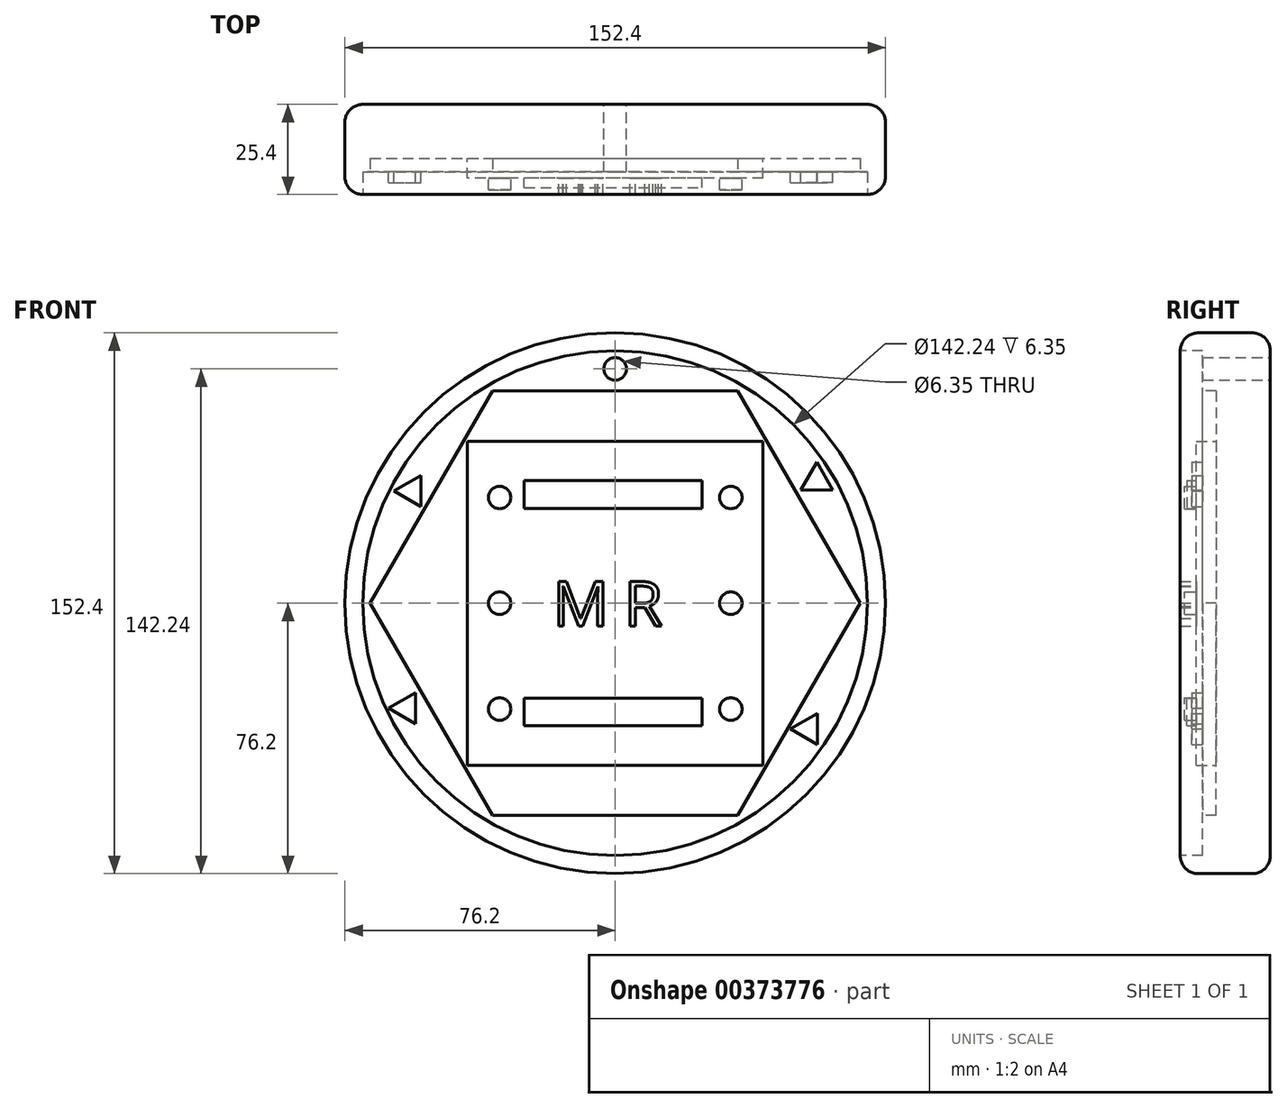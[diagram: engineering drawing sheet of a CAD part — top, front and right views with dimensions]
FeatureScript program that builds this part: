
annotation { "Feature Type Name" : "Feature", "Feature Type Description" : "" }
export const myFeature = defineFeature(function(context is Context, id is Id, definition is map)
    precondition{}
    {
        {
            var Q0;
            Q0=qCreatedBy(makeId("Front.planeOp"),FACE);
            var sketch = newSketch(context, id + "F0", { "sketchPlane" : qUnion([Q0])});
            skCircle(sketch, "E0", {"center": v(0, 0) * mm, "radius": 76.2 * mm});
            skSolve(sketch);
        }
        {
            var Q0;
            Q0 = qSketchRegion(id + "F0", true);
            extrude(context, id + "F1", {"entities" : qUnion([Q0]), "depth" : 25.4 * mm});
        }
        {
            var Q0;
            Q0=makeQuery(id+"F1.opExtrude","CAP_EDGE",EDGE,{"disambiguationData":[OSD([sQuery(id+"F0.wireOp",EDGE,"E0")])],"isStart":false});
            var Q1;
            Q1=makeQuery(id+"F1.opExtrude","CAP_EDGE",EDGE,{"disambiguationData":[OSD([sQuery(id+"F0.wireOp",EDGE,"E0")])],"isStart":true});
            fillet(context, id + "F2", {"entities" : qUnion([Q0, Q1]), "radius" : 5.08 * mm, "tangentPropagation" : true, "allowEdgeOverflow" : false});
        }
        {
            var Q0;
            Q0=makeQuery(id+"F1.opExtrude","CAP_FACE",FACE,{"disambiguationData":[OSD([sQuery(id+"F0.wireOp",EDGE,"E0")])],"isStart":false});
            extrude(context, id + "F3", {"entities" : qUnion([Q0]), "operationType" : NewBodyOperationType.REMOVE, "oppositeDirection" : true, "depth" : 6.35 * mm});
        }
        {
            var Q0;
            Q0=makeQuery(id+"F3.boolean.opBoolean","COPY",FACE,{"derivedFrom":makeQuery(id+"F3.opExtrude","CAP_FACE",FACE,{"disambiguationData":[OSD([sQuery(id+"F0.wireOp",EDGE,"E0")])],"isStart":false})});
            var sketch = newSketch(context, id + "F4", { "sketchPlane" : qUnion([Q0])});
            skText(sketch, "E1", { "text": "M", "fontName": "OpenSans-Regular.ttf"});
            const initialGuessF4  = {"E1": [-0.01767, -0.00645, 1, 0, 0.0127]};
            skSetInitialGuess(sketch, initialGuessF4);
            skSolve(sketch);
        }
        {
            var Q0;
            Q0=makeQuery(id+"F3.boolean.opBoolean","COPY",FACE,{"derivedFrom":makeQuery(id+"F3.opExtrude","CAP_FACE",FACE,{"disambiguationData":[OSD([sQuery(id+"F0.wireOp",EDGE,"E0")])],"isStart":false})});
            var sketch = newSketch(context, id + "F5", { "sketchPlane" : qUnion([Q0])});
            skText(sketch, "E2", { "text": "R", "fontName": "OpenSans-Regular.ttf"});
            const initialGuessF5  = {"E2": [0.0025, -0.00648, 1, 0, 0.0127]};
            skSetInitialGuess(sketch, initialGuessF5);
            skSolve(sketch);
        }
        {
            var Q0;
            Q0=qCreatedBy(makeId("Front.planeOp"),FACE);
            var sketch = newSketch(context, id + "F6", { "sketchPlane" : qUnion([Q0])});
            skCircle(sketch, "E3", {"center": v(0, 66.04) * mm, "radius": 3.18 * mm});
            skSolve(sketch);
        }
        {
            var Q0;
            Q0=sQuery(id+"F6.wireOp",VERTEX,"E3.center");
            var Q1;
            Q1=makeQuery(id+"F1.opExtrude","SWEPT_BODY",BODY,{"disambiguationData":[OSD([sQuery(id+"F0.wireOp",EDGE,"E0")])]});
            hole(context, id + "F7", {"style" : HoleStyle.SIMPLE, "endStyle" : HoleEndStyle.THROUGH, "oppositeDirection" : true, "holeDiameter" : 6.35 * mm, "isTappedThrough" : true, "tappedDepth" : 12.7 * mm, "tapClearance" : 3, "locations" : qUnion([Q0]), "scope" : qUnion([Q1])});
        }
        {
            var Q0;
            Q0=makeQuery(id+"F3.boolean.opBoolean","COPY",FACE,{"derivedFrom":makeQuery(id+"F3.opExtrude","CAP_FACE",FACE,{"disambiguationData":[OSD([sQuery(id+"F0.wireOp",EDGE,"E0")])],"isStart":false})});
            var sketch = newSketch(context, id + "F8", { "sketchPlane" : qUnion([Q0])});
            skCircle(sketch, "E4", {"center": v(-32.59, -29.81) * mm, "radius": 3.18 * mm});
            skCircle(sketch, "E5", {"center": v(-32.59, 0) * mm, "radius": 3.18 * mm});
            skCircle(sketch, "E6", {"center": v(-32.59, 29.82) * mm, "radius": 3.18 * mm});
            skCircle(sketch, "E7", {"center": v(32.59, -29.82) * mm, "radius": 3.18 * mm});
            skCircle(sketch, "E8", {"center": v(32.59, 0) * mm, "radius": 3.18 * mm});
            skCircle(sketch, "E9", {"center": v(32.59, 29.82) * mm, "radius": 3.18 * mm});
            skSolve(sketch);
        }
        {
            var Q0;
            Q0 = qSketchRegion(id + "F8", true);
            extrude(context, id + "F9", {"entities" : qUnion([Q0]), "depth" : 5.08 * mm, "offsetDistance" : 25.4 * mm});
        }
        {
            var Q0;
            Q0=qCreatedBy(makeId("Front.planeOp"),FACE);
            var sketch = newSketch(context, id + "F10", { "sketchPlane" : qUnion([Q0])});
            skCircle(sketch, "E10.cCircle", {"center": v(0, 0) * mm, "radius": 59.82 * mm, "construction": true});
            skLineSegment(sketch, "E10.0", {"start": v(34.54, 59.82) * mm, "end": v(69.08, 0) * mm});
            skLineSegment(sketch, "E10.1", {"start": v(69.08, 0) * mm, "end": v(34.54, -59.82) * mm});
            skLineSegment(sketch, "E10.2", {"start": v(34.54, -59.82) * mm, "end": v(-34.54, -59.82) * mm});
            skLineSegment(sketch, "E10.3", {"start": v(-34.54, -59.82) * mm, "end": v(-69.08, 0) * mm});
            skLineSegment(sketch, "E10.4", {"start": v(-69.08, 0) * mm, "end": v(-34.54, 59.82) * mm});
            skLineSegment(sketch, "E10.5", {"start": v(-34.54, 59.82) * mm, "end": v(34.54, 59.82) * mm});
            skPoint(sketch, "E10.0.midPoint", {"position": v(51.8, 29.91) * mm});
            skSolve(sketch);
        }
        {
            var Q0;
            Q0 = qSketchRegion(id + "F10", true);
            extrude(context, id + "F11", {"entities" : qUnion([Q0]), "operationType" : NewBodyOperationType.ADD, "depth" : 20.32 * mm});
        }
        {
            var Q0;
            Q0=qCreatedBy(makeId("Front.planeOp"),FACE);
            var sketch = newSketch(context, id + "F12", { "sketchPlane" : qUnion([Q0])});
            skLineSegment(sketch, "E11.bottom", {"start": v(41.68, -45.62) * mm, "end": v(-41.68, -45.62) * mm});
            skLineSegment(sketch, "E11.top", {"start": v(41.68, 45.62) * mm, "end": v(-41.68, 45.62) * mm});
            skLineSegment(sketch, "E11.left", {"start": v(41.68, -45.62) * mm, "end": v(41.68, 45.62) * mm});
            skLineSegment(sketch, "E11.right", {"start": v(-41.68, -45.62) * mm, "end": v(-41.68, 45.62) * mm});
            skPoint(sketch, "E11.middle", {"position": v(0, 0) * mm});
            skSolve(sketch);
        }
        {
            var Q0;
            Q0 = qSketchRegion(id + "F12", true);
            extrude(context, id + "F13", {"entities" : qUnion([Q0]), "operationType" : NewBodyOperationType.ADD, "depth" : 20.83 * mm, "offsetDistance" : 25.4 * mm});
        }
        {
            var Q0;
            Q0=qCreatedBy(makeId("Front.planeOp"),FACE);
            var sketch = newSketch(context, id + "F14", { "sketchPlane" : qUnion([Q0])});
            skCircle(sketch, "E12.cCircle", {"center": v(56.84, 34.54) * mm, "radius": 2.62 * mm, "construction": true});
            skLineSegment(sketch, "E12.0", {"start": v(61.38, 31.92) * mm, "end": v(52.3, 31.92) * mm});
            skLineSegment(sketch, "E12.1", {"start": v(52.3, 31.92) * mm, "end": v(56.84, 39.79) * mm});
            skLineSegment(sketch, "E12.2", {"start": v(56.84, 39.79) * mm, "end": v(61.38, 31.92) * mm});
            skPoint(sketch, "E12.0.midPoint", {"position": v(56.84, 31.92) * mm});
            skSolve(sketch);
        }
        {
            var Q0;
            Q0 = qSketchRegion(id + "F14", true);
            extrude(context, id + "F15", {"entities" : qUnion([Q0]), "operationType" : NewBodyOperationType.ADD, "depth" : 22.1 * mm});
        }
        {
            var Q0;
            Q0=qCreatedBy(makeId("Front.planeOp"),FACE);
            var sketch = newSketch(context, id + "F16", { "sketchPlane" : qUnion([Q0])});
            skCircle(sketch, "E13.cCircle", {"center": v(54.46, -35.41) * mm, "radius": 2.54 * mm, "construction": true});
            skLineSegment(sketch, "E13.0", {"start": v(57, -31.01) * mm, "end": v(57, -39.81) * mm});
            skLineSegment(sketch, "E13.1", {"start": v(57, -39.81) * mm, "end": v(49.38, -35.41) * mm});
            skLineSegment(sketch, "E13.2", {"start": v(49.38, -35.41) * mm, "end": v(57, -31.01) * mm});
            skPoint(sketch, "E13.0.midPoint", {"position": v(57, -35.41) * mm});
            skSolve(sketch);
        }
        {
            var Q0;
            Q0 = qSketchRegion(id + "F16", true);
            extrude(context, id + "F17", {"entities" : qUnion([Q0]), "operationType" : NewBodyOperationType.ADD, "depth" : 22.1 * mm});
        }
        {
            var Q0;
            Q0=qCreatedBy(makeId("Front.planeOp"),FACE);
            var sketch = newSketch(context, id + "F18", { "sketchPlane" : qUnion([Q0])});
            skCircle(sketch, "E14.cCircle", {"center": v(-57.32, 31.63) * mm, "radius": 2.54 * mm, "construction": true});
            skLineSegment(sketch, "E14.0", {"start": v(-54.78, 36.02) * mm, "end": v(-54.78, 27.23) * mm});
            skLineSegment(sketch, "E14.1", {"start": v(-54.78, 27.23) * mm, "end": v(-62.4, 31.63) * mm});
            skLineSegment(sketch, "E14.2", {"start": v(-62.4, 31.63) * mm, "end": v(-54.78, 36.02) * mm});
            skPoint(sketch, "E14.0.midPoint", {"position": v(-54.78, 31.63) * mm});
            skSolve(sketch);
        }
        {
            var Q0;
            Q0 = qSketchRegion(id + "F18", true);
            extrude(context, id + "F19", {"entities" : qUnion([Q0]), "operationType" : NewBodyOperationType.ADD, "depth" : 22.1 * mm});
        }
        {
            var Q0;
            Q0=qCreatedBy(makeId("Front.planeOp"),FACE);
            var sketch = newSketch(context, id + "F20", { "sketchPlane" : qUnion([Q0])});
            skCircle(sketch, "E15.cCircle", {"center": v(-58.77, -29.58) * mm, "radius": 2.54 * mm, "construction": true});
            skLineSegment(sketch, "E15.0", {"start": v(-56.23, -25.19) * mm, "end": v(-56.23, -33.98) * mm});
            skLineSegment(sketch, "E15.1", {"start": v(-56.23, -33.98) * mm, "end": v(-63.85, -29.58) * mm});
            skLineSegment(sketch, "E15.2", {"start": v(-63.85, -29.58) * mm, "end": v(-56.23, -25.19) * mm});
            skPoint(sketch, "E15.0.midPoint", {"position": v(-56.23, -29.58) * mm});
            skSolve(sketch);
        }
        {
            var Q0;
            Q0 = qSketchRegion(id + "F20", true);
            extrude(context, id + "F21", {"entities" : qUnion([Q0]), "operationType" : NewBodyOperationType.ADD, "depth" : 22.1 * mm});
        }
        {
            var Q0;
            {var subQ0=sQuery(id+"F10.wireOp",EDGE,"E10.0");var subQ1=sQuery(id+"F10.wireOp",EDGE,"E10.1");var subQ2=sQuery(id+"F10.wireOp",EDGE,"E10.4");var subQ3=sQuery(id+"F10.wireOp",EDGE,"E10.2");var subQ4=sQuery(id+"F10.wireOp",EDGE,"E10.3");var subQ5=sQuery(id+"F10.wireOp",EDGE,"E10.5");Q0=makeQuery(id+"F11.boolean.opBoolean","SPLIT",FACE,{"disambiguationData":[TD([makeQuery(id+"FFlFKEa7tA48LvB_1.opExtrude","SWEPT_FACE",FACE,{"disambiguationData":[OSD([sQuery(id+"F4.wireOp",EDGE,"E1.sketch_text.stroke-0")])]})])],"derivedFrom":makeQuery(id+"F11.opExtrude","CAP_FACE",FACE,{"disambiguationData":[OSD([subQ0,subQ1,subQ3,subQ4,subQ2,subQ5])],"isStart":false})});}
            var sketch = newSketch(context, id + "F22", { "sketchPlane" : qUnion([Q0])});
            skCircle(sketch, "E16", {"center": v(0, 0) * mm, "radius": 26.77 * mm});
            skSolve(sketch);
        }
        {
            var Q0;
            Q0=sQuery(id+"F22.wireOp",EDGE,"E16");
            extrude(context, id + "F23", {"bodyType" : ToolBodyType.SURFACE, "surfaceEntities" : qUnion([Q0]), "depth" : 3.17 * mm});
        }
        {
            var Q0;
            {var subQ0=sQuery(id+"F10.wireOp",EDGE,"E10.0");var subQ1=sQuery(id+"F10.wireOp",EDGE,"E10.1");var subQ2=sQuery(id+"F10.wireOp",EDGE,"E10.4");var subQ3=sQuery(id+"F10.wireOp",EDGE,"E10.2");var subQ4=sQuery(id+"F10.wireOp",EDGE,"E10.3");var subQ5=sQuery(id+"F10.wireOp",EDGE,"E10.5");Q0=makeQuery(id+"F11.boolean.opBoolean","SPLIT",FACE,{"disambiguationData":[TD([makeQuery(id+"FFlFKEa7tA48LvB_1.opExtrude","SWEPT_FACE",FACE,{"disambiguationData":[OSD([sQuery(id+"F4.wireOp",EDGE,"E1.sketch_text.stroke-0")])]})])],"derivedFrom":makeQuery(id+"F11.opExtrude","CAP_FACE",FACE,{"disambiguationData":[OSD([subQ0,subQ1,subQ3,subQ4,subQ2,subQ5])],"isStart":false})});}
            var sketch = newSketch(context, id + "F24", { "sketchPlane" : qUnion([Q0])});
            skLineSegment(sketch, "E17.bottom", {"start": v(-25.61, 34.54) * mm, "end": v(24.47, 34.54) * mm});
            skLineSegment(sketch, "E17.top", {"start": v(-25.61, 26.77) * mm, "end": v(24.47, 26.77) * mm});
            skLineSegment(sketch, "E17.left", {"start": v(-25.61, 34.54) * mm, "end": v(-25.61, 26.77) * mm});
            skLineSegment(sketch, "E17.right", {"start": v(24.47, 34.54) * mm, "end": v(24.47, 26.77) * mm});
            skLineSegment(sketch, "E18.bottom", {"start": v(-25.61, -34.54) * mm, "end": v(24.47, -34.54) * mm});
            skLineSegment(sketch, "E18.top", {"start": v(-25.61, -26.77) * mm, "end": v(24.47, -26.77) * mm});
            skLineSegment(sketch, "E18.left", {"start": v(-25.61, -34.54) * mm, "end": v(-25.61, -26.77) * mm});
            skLineSegment(sketch, "E18.right", {"start": v(24.47, -34.54) * mm, "end": v(24.47, -26.77) * mm});
            skSolve(sketch);
        }
        {
            var Q0;
            Q0 = qSketchRegion(id + "F24", true);
            extrude(context, id + "F25", {"entities" : qUnion([Q0]), "operationType" : NewBodyOperationType.ADD, "depth" : 3.17 * mm});
        }
        {
            var Q0;
            Q0 = qSketchRegion(id + "F4", true);
            extrude(context, id + "F26", {"entities" : qUnion([Q0]), "operationType" : NewBodyOperationType.ADD, "depth" : 6.35 * mm});
        }
        {
            var Q0;
            Q0 = qSketchRegion(id + "F5", true);
            extrude(context, id + "F27", {"entities" : qUnion([Q0]), "operationType" : NewBodyOperationType.ADD, "depth" : 6.35 * mm});
        }
        {
            var Q0;
            Q0=makeQuery(id+"F11.opExtrude","CAP_FACE",FACE,{"disambiguationData":[OSD([sQuery(id+"F10.wireOp",EDGE,"E10.0"),sQuery(id+"F10.wireOp",EDGE,"E10.1"),sQuery(id+"F10.wireOp",EDGE,"E10.2"),sQuery(id+"F10.wireOp",EDGE,"E10.3"),sQuery(id+"F10.wireOp",EDGE,"E10.4"),sQuery(id+"F10.wireOp",EDGE,"E10.5")])],"isStart":false});
            extrude(context, id + "F28", {"entities" : qUnion([Q0]), "operationType" : NewBodyOperationType.REMOVE, "oppositeDirection" : true, "depth" : 5.08 * mm});
        }
    });
